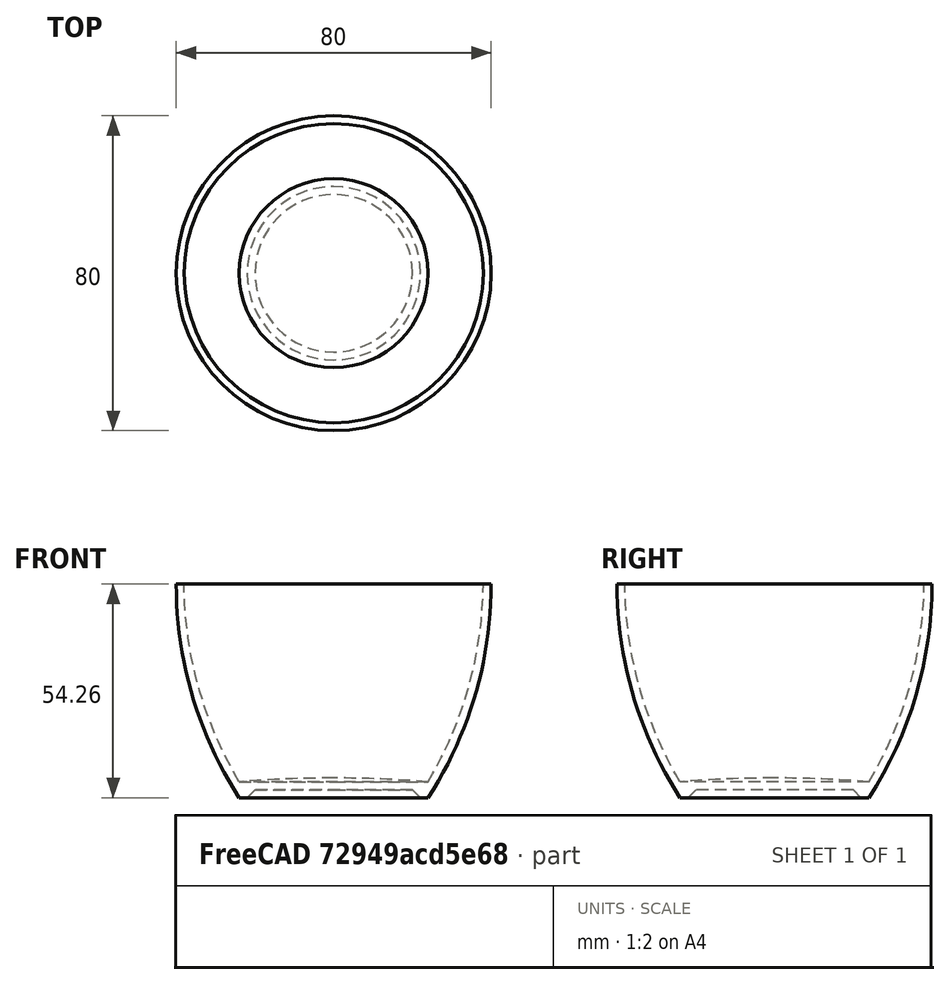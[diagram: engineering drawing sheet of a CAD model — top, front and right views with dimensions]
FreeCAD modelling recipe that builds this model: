
FCSTD DOCUMENT  (FreeCAD 0.18R4 (GitTag))
Label: l 9 q2
License: All rights reserved
LicenseURL: http://en.wikipedia.org/wiki/All_rights_reserved
objects: TechDraw::DrawViewDimension×5, PartDesign::Body×2, TechDraw::DrawProjGroupItem×2, Sketcher::SketchObject×1, PartDesign::Revolution×1, TechDraw::DrawSVGTemplate×1, TechDraw::DrawProjGroup×1, TechDraw::DrawViewSection×1, TechDraw::DrawPage×1
note: 5 computed .brp shape members not serialized (recipe doc carries the construction recipe); baked Part::Feature solids carry a one-line shape summary decoded from their .brp

FEATURE [PartDesign::Body] Body
  Origin = -> Origin
FEATURE [Sketcher::SketchObject] Sketch
  MapMode = 5
  Placement = pos=(0,0,0) rot=(0.57735,0.57735,0.57735;2.0944rad)
  Support = -> [YZ_Plane001]
  sketch-geometry (8):
    g0: LineSegment StartX=0 StartY=0 StartZ=0 EndX=20 EndY=0 EndZ=0
    g1: LineSegment StartX=20 StartY=0 StartZ=0 EndX=22 EndY=-2 EndZ=0
    g2: LineSegment StartX=22 StartY=-2 StartZ=0 EndX=24 EndY=-2 EndZ=0
    g3: ArcOfCircle CenterX=0 CenterY=-297 CenterZ=0 NormalX=0 NormalY=0 NormalZ=1 AngleXU=0 Radius=300 StartAngle=1.49071 EndAngle=1.5708
    g4: ArcOfCircle CenterX=-60 CenterY=52.2586 CenterZ=0 NormalX=0 NormalY=0 NormalZ=1 AngleXU=0 Radius=100 StartAngle=5.70967 EndAngle=6.28319
    g5: LineSegment StartX=38 StartY=52.2586 StartZ=0 EndX=40 EndY=52.2586 EndZ=0
    g6: ArcOfCircle CenterX=-61.9967 CenterY=53.0735 CenterZ=0 NormalX=0 NormalY=0 NormalZ=1 AngleXU=0 Radius=100 StartAngle=5.74759 EndAngle=6.27504
    g7: LineSegment StartX=1.84e-14 StartY=3 StartZ=0 EndX=0 EndY=0 EndZ=0
  constraints (26):
    c: Horizontal(g0)
    c: Coincident(g0,g-1)
    c: Distance(g0) = 20
    c: Coincident(g1,g0)
    c: DistanceX(g0,g1) = 2
    c: DistanceY(g1,g0) = 2
    c: Coincident(g2,g1)
    c: Horizontal(g2)
    c: Distance(g2) = 2
    c: DistanceY(g0,g3) = 3
    c: DistanceX(g0,g3) = 0
    c: DistanceY(g3,g0) = 297
    c: DistanceX(g0,g3) = 0
    c: DistanceX(g3,g3) = 24
    c: Coincident(g4,g2)
    c: DistanceY(g4,g4) = 0
    c: Radius(g4) = 100
    c: DistanceX(g4,g0) = 60
    c: Coincident(g5,g4)
    c: Horizontal(g5)
    c: Distance(g5) = 2
    c: Coincident(g6,g5)
    c: Coincident(g6,g3)
    c: Radius(g6) = 100
    c: Coincident(g7,g3)
    c: Coincident(g7,g0)
FEATURE [PartDesign::Revolution] Revolution
  Angle = 360
  Axis = (-2e-16,3e-16,1)
  Base = (0,0,0)
  Placement = pos=(0,0,0) rot=(0.57735,0.57735,0.57735;2.0944rad)
  Profile = -> Sketch
  ReferenceAxis = -> Sketch [V_Axis]
  Reversed = true
FEATURE [PartDesign::Body] Body001
  Group = -> [Sketch,Revolution]
  Origin = -> Origin001
  Tip = -> Revolution
FEATURE [TechDraw::DrawSVGTemplate] Template
  EditableTexts = AUTHOR_NAME=AUTHOR NAME; DN=DN; DRAWING_TITLE=DRAWING TITLE; FC-DATE=DD/MM/YYYY; FC-REV=REV A; FC-SC=SCALE; FC-SH=X / Y; FC-SI=A2; FreeCAD_DRAWING=FreeCAD DRAWING; PN=PN
  Height = 420
  Orientation = 1
  Width = 594
FEATURE [TechDraw::DrawProjGroupItem] ProjItem  label="Front"
  CoarseView = false
  Direction = (0,-1,0)
  Focus = 100
  HardHidden = false
  IsoCount = 0
  IsoHidden = false
  IsoVisible = false
  LockPosition = true
  Perspective = false
  Rotation = 0
  RotationVector = (1,0,0)
  Scale = 2
  ScaleType = 2
  SeamHidden = false
  SeamVisible = false
  SmoothHidden = false
  SmoothVisible = false
  Source = -> [Body001]
  Type = 0
  X = 0
  Y = 0
FEATURE [TechDraw::DrawProjGroupItem] ProjItem001  label="Bottom"
  CoarseView = false
  Direction = (0,0,-1)
  Focus = 100
  HardHidden = false
  IsoCount = 0
  IsoHidden = false
  IsoVisible = false
  LockPosition = false
  Perspective = false
  Rotation = 0
  RotationVector = (1,0,0)
  Scale = 2
  ScaleType = 2
  SeamHidden = false
  SeamVisible = false
  SmoothHidden = false
  SmoothVisible = false
  Source = -> [Body001]
  Type = 5
  X = 0
  Y = 175
FEATURE [TechDraw::DrawProjGroup] ProjGroup
  Anchor = -> ProjItem
  AutoDistribute = true
  LockPosition = false
  ProjectionType = 0
  Rotation = 0
  Scale = 2
  ScaleType = 0
  Source = -> [Body001]
  Views = -> [ProjItem,ProjItem001]
  X = 226.653
  Y = 121.935
  spacingX = 15
  spacingY = 15
FEATURE [TechDraw::DrawViewSection] Section  label="Section A - A"
  BaseView = -> ProjItem001
  CoarseView = false
  Direction = (0,1,0)
  Focus = 100
  FuseBeforeCut = true
  HardHidden = false
  HatchScale = 1
  IsoCount = 0
  IsoHidden = false
  IsoVisible = false
  LockPosition = false
  NameGeomPattern = Diamond
  Perspective = false
  Rotation = 0
  Scale = 2
  ScaleType = 2
  SeamHidden = false
  SeamVisible = false
  SectionDirection = 2
  SectionNormal = (0,1,0)
  SectionOrigin = (0,2.13e-14,25.13)
  SectionSymbol = A
  SmoothHidden = false
  SmoothVisible = false
  Source = -> [Body001]
  X = 447.097
  Y = 298.586
FEATURE [TechDraw::DrawViewDimension] Dimension
  Arbitrary = false
  FormatSpec = %.2f
  LockPosition = false
  MeasureType = 1
  OverTolerance = 0
  References2D = -> [Section]
  Rotation = 0
  Scale = 2
  ScaleType = 0
  Type = 1
  UnderTolerance = 0
  X = 0.521092
  Y = -85.1718
FEATURE [TechDraw::DrawViewDimension] Dimension001
  Arbitrary = false
  FormatSpec = %.2f
  LockPosition = false
  MeasureType = 1
  OverTolerance = 0
  References2D = -> [Section]
  Rotation = 0
  Scale = 2
  ScaleType = 0
  Type = 1
  UnderTolerance = 0
  X = 45.4789
  Y = -86.5663
FEATURE [TechDraw::DrawViewDimension] Dimension002
  Arbitrary = false
  FormatSpec = %.2f
  LockPosition = false
  MeasureType = 1
  OverTolerance = 0
  References2D = -> [Section]
  Rotation = 0
  Scale = 2
  ScaleType = 0
  Type = 1
  UnderTolerance = 0
  X = -43.0422
  Y = -82.482
FEATURE [TechDraw::DrawViewDimension] Dimension003
  Arbitrary = false
  FormatSpec = R%.2f
  LockPosition = false
  MeasureType = 1
  OverTolerance = 0
  References2D = -> [Section]
  Rotation = 0
  Scale = 2
  ScaleType = 0
  Type = 4
  UnderTolerance = 0
  X = -116.203
  Y = 20.3226
FEATURE [TechDraw::DrawViewDimension] Dimension004
  Arbitrary = false
  FormatSpec = R%.2f
  LockPosition = false
  MeasureType = 1
  OverTolerance = 0
  References2D = -> [Section]
  Rotation = 0
  Scale = 2
  ScaleType = 0
  Type = 4
  UnderTolerance = 0
  X = -102.134
  Y = -35.4342
FEATURE [TechDraw::DrawPage] Page
  KeepUpdated = true
  ProjectionType = 0
  Scale = 2
  Template = -> Template
  Views = -> [ProjGroup,Section,Dimension,Dimension001,Dimension002,Dimension003,Dimension004]
